annotation { "Feature Type Name" : "Feature", "Feature Type Description" : "" }
export const myFeature = defineFeature(function(context is Context, id is Id, definition is map)
    precondition{}
    {
        {
            var Q0;
            Q0=qCreatedBy(makeId("Front.planeOp"),FACE);
            var sketch = newSketch(context, id + "F0", { "sketchPlane" : qUnion([Q0])});
            skArc(sketch, "E0", {"start": v(0, -100.55) * mm, "mid": v(100.55, 0) * mm, "end": v(0, 100.55) * mm});
            skLineSegment(sketch, "E1", {"start": v(0, 0) * mm, "end": v(0, 121.6) * mm});
            skLineSegment(sketch, "E2", {"start": v(0, 0) * mm, "end": v(0, -100.55) * mm});
            skSolve(sketch);
        }
        {
            var Q0;
            Q0 = qSketchRegion(id + "F0", true);
            var Q1;
            Q1=sQuery(id+"F0.wireOp",EDGE,"E1");
            revolve(context, id + "F1", {"surfaceOperationType" : NewSurfaceOperationType.NEW, "entities" : qUnion([Q0]), "axis" : qUnion([Q1]), "revolveType" : RevolveType.FULL});
        }
        {
            var Q0;
            Q0=qCreatedBy(makeId("Right.planeOp"),FACE);
            var sketch = newSketch(context, id + "F2", { "sketchPlane" : qUnion([Q0])});
            skLineSegment(sketch, "E3.bottom", {"start": v(0, -120.65) * mm, "end": v(6045.2, -120.65) * mm});
            skLineSegment(sketch, "E3.top", {"start": v(0, -107.95) * mm, "end": v(6045.2, -107.95) * mm});
            skLineSegment(sketch, "E3.left", {"start": v(0, -120.65) * mm, "end": v(0, -107.95) * mm});
            skLineSegment(sketch, "E3.right", {"start": v(6045.2, -120.65) * mm, "end": v(6045.2, -107.95) * mm});
            skSolve(sketch);
        }
        {
            var Q0;
            Q0 = qSketchRegion(id + "F2", true);
            extrude(context, id + "F3", {"entities" : qUnion([Q0]), "depth" : 12.7 * mm, "offsetDistance" : 25.4 * mm});
        }
        {
            var Q0;
            Q0=makeQuery(id+"F3.opExtrude","CAP_FACE",FACE,{"disambiguationData":[OSD([sQuery(id+"F2.wireOp",EDGE,"E3.bottom"),sQuery(id+"F2.wireOp",EDGE,"E3.top"),sQuery(id+"F2.wireOp",EDGE,"E3.left"),sQuery(id+"F2.wireOp",EDGE,"E3.right")])],"isStart":true});
            var sketch = newSketch(context, id + "F4", { "sketchPlane" : qUnion([Q0])});
            skArc(sketch, "E4", {"start": v(-6045.12, -73.89) * mm, "mid": v(-6017.65, -46.52) * mm, "end": v(-6045.02, -19.05) * mm});
            skLineSegment(sketch, "E5", {"start": v(-6045.2, -120.65) * mm, "end": v(-6045.02, -19.05) * mm});
            skSolve(sketch);
        }
        {
            var Q0;
            Q0 = qSketchRegion(id + "F4", true);
            var Q1;
            Q1=sQuery(id+"F4.wireOp",EDGE,"E5");
            revolve(context, id + "F5", {"surfaceOperationType" : NewSurfaceOperationType.NEW, "entities" : qUnion([Q0]), "axis" : qUnion([Q1]), "revolveType" : RevolveType.FULL});
        }
        {
            var Q0;
            Q0=makeQuery(id+"F3.opExtrude","CAP_FACE",FACE,{"disambiguationData":[OSD([sQuery(id+"F2.wireOp",EDGE,"E3.bottom"),sQuery(id+"F2.wireOp",EDGE,"E3.top"),sQuery(id+"F2.wireOp",EDGE,"E3.left"),sQuery(id+"F2.wireOp",EDGE,"E3.right")])],"isStart":true});
            var sketch = newSketch(context, id + "F6", { "sketchPlane" : qUnion([Q0])});
            skLineSegment(sketch, "E6", {"start": v(-6045.2, -120.65) * mm, "end": v(-6045.2, -69.85) * mm});
            skLineSegment(sketch, "E7", {"start": v(-6045.2, -69.85) * mm, "end": v(-5957.21, -120.65) * mm});
            skLineSegment(sketch, "E8", {"start": v(0, -120.65) * mm, "end": v(0, -69.85) * mm});
            skLineSegment(sketch, "E9", {"start": v(0, -69.85) * mm, "end": v(-87.99, -120.65) * mm});
            skLineSegment(sketch, "E10", {"start": v(-87.99, -120.65) * mm, "end": v(0, -120.65) * mm});
            skLineSegment(sketch, "E11", {"start": v(-6045.2, -120.65) * mm, "end": v(-5957.21, -120.65) * mm});
            skSolve(sketch);
        }
        {
            var Q0;
            Q0 = qSketchRegion(id + "F6", true);
            extrude(context, id + "F7", {"entities" : qUnion([Q0]), "operationType" : NewBodyOperationType.ADD, "depth" : 12.7 * mm, "offsetDistance" : 25.4 * mm, "hasSecondDirection" : true, "secondDirectionOppositeDirection" : true, "secondDirectionDepth" : 12.7 * mm});
        }
        {
            var Q0;
            Q0=makeQuery(id+"F3.opExtrude","CAP_FACE",FACE,{"disambiguationData":[OSD([sQuery(id+"F2.wireOp",EDGE,"E3.bottom"),sQuery(id+"F2.wireOp",EDGE,"E3.top"),sQuery(id+"F2.wireOp",EDGE,"E3.left"),sQuery(id+"F2.wireOp",EDGE,"E3.right")])],"isStart":true});
            extrude(context, id + "F8", {"entities" : qUnion([Q0]), "operationType" : NewBodyOperationType.ADD, "depth" : 12.7 * mm, "offsetDistance" : 25.4 * mm});
        }
        {
            var Q0;
            {var subQ0=sQuery(id+"F2.wireOp",EDGE,"E3.top");Q0=makeQuery(id+"F8.boolean.opBoolean","MERGE",FACE,{"derivedFrom":[makeQuery(id+"F3.opExtrude","SWEPT_FACE",FACE,{"disambiguationData":[OSD([subQ0])]}),makeQuery(id+"F8.opExtrude","SWEPT_FACE",FACE,{"disambiguationData":[OSD([subQ0])]})]});}
            var sketch = newSketch(context, id + "F9", { "sketchPlane" : qUnion([Q0])});
            skLineSegment(sketch, "E12.bottom", {"start": v(-12.7, 101.6) * mm, "end": v(12.7, 101.6) * mm});
            skLineSegment(sketch, "E12.top", {"start": v(-12.7, 104.14) * mm, "end": v(12.7, 104.14) * mm});
            skLineSegment(sketch, "E12.left", {"start": v(-12.7, 101.6) * mm, "end": v(-12.7, 104.14) * mm});
            skLineSegment(sketch, "E12.right", {"start": v(12.7, 101.6) * mm, "end": v(12.7, 104.14) * mm});
            skSolve(sketch);
        }
        {
            var Q0;
            Q0 = qSketchRegion(id + "F9", true);
            extrude(context, id + "F10", {"entities" : qUnion([Q0]), "operationType" : NewBodyOperationType.REMOVE, "oppositeDirection" : true, "depth" : 2.54 * mm, "offsetDistance" : 25.4 * mm});
        }
        {
            var Q0;
            Q0=makeQuery(id+"F7.boolean.opBoolean","MERGE",FACE,{"derivedFrom":[makeQuery(id+"F3.opExtrude","CAP_FACE",FACE,{"disambiguationData":[OSD([sQuery(id+"F2.wireOp",EDGE,"E3.bottom"),sQuery(id+"F2.wireOp",EDGE,"E3.top"),sQuery(id+"F2.wireOp",EDGE,"E3.left"),sQuery(id+"F2.wireOp",EDGE,"E3.right")])],"isStart":false}),makeQuery(id+"F7.opExtrude","CAP_FACE",FACE,{"disambiguationData":[OSD([sQuery(id+"F6.wireOp",EDGE,"E6"),sQuery(id+"F6.wireOp",EDGE,"E7"),sQuery(id+"F6.wireOp",EDGE,"E11")])],"isStart":true}),makeQuery(id+"F7.opExtrude","CAP_FACE",FACE,{"disambiguationData":[OSD([sQuery(id+"F6.wireOp",EDGE,"E8"),sQuery(id+"F6.wireOp",EDGE,"E9"),sQuery(id+"F6.wireOp",EDGE,"E10")])],"isStart":true})]});
            var sketch = newSketch(context, id + "F11", { "sketchPlane" : qUnion([Q0])});
            skText(sketch, "E13", { "text": "          Low Earth Orbit\n(International Space Station)", "fontName": "OpenSans-Regular.ttf"});
            const initialGuessF11  = {"E13": [0.08123, -0.11366, 1, 0, 0.00254]};
            skSetInitialGuess(sketch, initialGuessF11);
            skSolve(sketch);
        }
        {
            var Q0;
            Q0 = qSketchRegion(id + "F11", true);
            extrude(context, id + "F12", {"entities" : qUnion([Q0]), "operationType" : NewBodyOperationType.REMOVE, "oppositeDirection" : true, "depth" : 2.54 * mm, "offsetDistance" : 25.4 * mm});
        }
        {
            var Q0;
            {var subQ0=sQuery(id+"F2.wireOp",EDGE,"E3.right");var subQ3=sQuery(id+"F2.wireOp",EDGE,"E3.left");var subQ4=sQuery(id+"F2.wireOp",EDGE,"E3.top");var subQ5=sQuery(id+"F2.wireOp",EDGE,"E3.bottom");var subQ6=sQuery(id+"F6.wireOp",EDGE,"E11");var subQ7=sQuery(id+"F6.wireOp",EDGE,"E10");var subQ8=sQuery(id+"F6.wireOp",EDGE,"E7");var subQ9=sQuery(id+"F6.wireOp",EDGE,"E8");var subQ10=sQuery(id+"F6.wireOp",EDGE,"E9");var subQ11=sQuery(id+"F6.wireOp",EDGE,"E6");Q0=makeQuery(id+"F12.boolean.opBoolean","SPLIT",FACE,{"disambiguationData":[TD([makeQuery(id+"F1.opRevolve","SWEPT_FACE",FACE,{"disambiguationData":[OSD([sQuery(id+"F0.wireOp",EDGE,"E0")])]})])],"derivedFrom":makeQuery(id+"F7.boolean.opBoolean","MERGE",FACE,{"derivedFrom":[makeQuery(id+"F3.opExtrude","CAP_FACE",FACE,{"disambiguationData":[OSD([subQ5,subQ4,subQ3,subQ0])],"isStart":false}),makeQuery(id+"F7.opExtrude","CAP_FACE",FACE,{"disambiguationData":[OSD([subQ11,subQ8,subQ6])],"isStart":true}),makeQuery(id+"F7.opExtrude","CAP_FACE",FACE,{"disambiguationData":[OSD([subQ9,subQ10,subQ7])],"isStart":true})]})});}
            var sketch = newSketch(context, id + "F13", { "sketchPlane" : qUnion([Q0])});
            skLineSegment(sketch, "E14.bottom", {"start": v(660.4, -107.95) * mm, "end": v(662.94, -107.95) * mm});
            skLineSegment(sketch, "E14.top", {"start": v(660.4, -110.49) * mm, "end": v(662.94, -110.49) * mm});
            skLineSegment(sketch, "E14.left", {"start": v(660.4, -107.95) * mm, "end": v(660.4, -110.49) * mm});
            skLineSegment(sketch, "E14.right", {"start": v(662.94, -107.95) * mm, "end": v(662.94, -110.49) * mm});
            skSolve(sketch);
        }
        {
            var Q0;
            Q0 = qSketchRegion(id + "F13", true);
            extrude(context, id + "F14", {"entities" : qUnion([Q0]), "operationType" : NewBodyOperationType.REMOVE, "endBound" : BoundingType.THROUGH_ALL, "oppositeDirection" : true, "depth" : 25.4 * mm, "offsetDistance" : 25.4 * mm});
        }
        {
            var Q0;
            {var subQ0=sQuery(id+"F2.wireOp",EDGE,"E3.right");var subQ3=sQuery(id+"F2.wireOp",EDGE,"E3.left");var subQ4=sQuery(id+"F2.wireOp",EDGE,"E3.top");var subQ5=sQuery(id+"F2.wireOp",EDGE,"E3.bottom");var subQ6=sQuery(id+"F6.wireOp",EDGE,"E11");var subQ7=sQuery(id+"F6.wireOp",EDGE,"E10");var subQ8=sQuery(id+"F6.wireOp",EDGE,"E7");var subQ9=sQuery(id+"F6.wireOp",EDGE,"E8");var subQ10=sQuery(id+"F6.wireOp",EDGE,"E9");var subQ11=sQuery(id+"F6.wireOp",EDGE,"E6");Q0=makeQuery(id+"F12.boolean.opBoolean","SPLIT",FACE,{"disambiguationData":[TD([makeQuery(id+"F1.opRevolve","SWEPT_FACE",FACE,{"disambiguationData":[OSD([sQuery(id+"F0.wireOp",EDGE,"E0")])]})])],"derivedFrom":makeQuery(id+"F7.boolean.opBoolean","MERGE",FACE,{"derivedFrom":[makeQuery(id+"F3.opExtrude","CAP_FACE",FACE,{"disambiguationData":[OSD([subQ5,subQ4,subQ3,subQ0])],"isStart":false}),makeQuery(id+"F7.opExtrude","CAP_FACE",FACE,{"disambiguationData":[OSD([subQ11,subQ8,subQ6])],"isStart":true}),makeQuery(id+"F7.opExtrude","CAP_FACE",FACE,{"disambiguationData":[OSD([subQ9,subQ10,subQ7])],"isStart":true})]})});}
            var sketch = newSketch(context, id + "F15", { "sketchPlane" : qUnion([Q0])});
            skText(sketch, "E15", { "text": "     Geosynchronous Orbit\n(GPS and Television Satellites)", "fontName": "OpenSans-Regular.ttf"});
            const initialGuessF15  = {"E15": [0.63754, -0.11366, 1, 0, 0.00254]};
            skSetInitialGuess(sketch, initialGuessF15);
            skSolve(sketch);
        }
        {
            var Q0;
            Q0 = qSketchRegion(id + "F15", true);
            extrude(context, id + "F16", {"entities" : qUnion([Q0]), "operationType" : NewBodyOperationType.REMOVE, "oppositeDirection" : true, "depth" : 2.54 * mm, "offsetDistance" : 25.4 * mm});
        }
        {
            var Q0;
            {var subQ278=sQuery(id+"F6.wireOp",EDGE,"E10");var subQ282=sQuery(id+"F6.wireOp",EDGE,"E7");var subQ290=sQuery(id+"F6.wireOp",EDGE,"E9");var subQ297=sQuery(id+"F6.wireOp",EDGE,"E6");var subQ304=sQuery(id+"F6.wireOp",EDGE,"E8");var subQ343=sQuery(id+"F2.wireOp",EDGE,"E3.right");var subQ356=sQuery(id+"F2.wireOp",EDGE,"E3.top");var subQ379=sQuery(id+"F6.wireOp",EDGE,"E11");var subQ384=sQuery(id+"F2.wireOp",EDGE,"E3.bottom");var subQ396=sQuery(id+"F2.wireOp",EDGE,"E3.left");var subQ507=makeQuery(id+"F1.opRevolve","SWEPT_FACE",FACE,{"disambiguationData":[OSD([sQuery(id+"F0.wireOp",EDGE,"E0")])]});Q0=makeQuery(id+"F16.boolean.opBoolean","SPLIT",FACE,{"disambiguationData":[TD([subQ507])],"derivedFrom":makeQuery(id+"F12.boolean.opBoolean","SPLIT",FACE,{"disambiguationData":[TD([subQ507])],"derivedFrom":makeQuery(id+"F7.boolean.opBoolean","MERGE",FACE,{"derivedFrom":[makeQuery(id+"F3.opExtrude","CAP_FACE",FACE,{"disambiguationData":[OSD([subQ384,subQ356,subQ396,subQ343])],"isStart":false}),makeQuery(id+"F7.opExtrude","CAP_FACE",FACE,{"disambiguationData":[OSD([subQ297,subQ282,subQ379])],"isStart":true}),makeQuery(id+"F7.opExtrude","CAP_FACE",FACE,{"disambiguationData":[OSD([subQ304,subQ290,subQ278])],"isStart":true})]})})});}
            var sketch = newSketch(context, id + "F17", { "sketchPlane" : qUnion([Q0])});
            skLineSegment(sketch, "E16.bottom", {"start": v(1143, -107.95) * mm, "end": v(1145.54, -107.95) * mm});
            skLineSegment(sketch, "E16.top", {"start": v(1143, -110.49) * mm, "end": v(1145.54, -110.49) * mm});
            skLineSegment(sketch, "E16.left", {"start": v(1143, -107.95) * mm, "end": v(1143, -110.49) * mm});
            skLineSegment(sketch, "E16.right", {"start": v(1145.54, -107.95) * mm, "end": v(1145.54, -110.49) * mm});
            skSolve(sketch);
        }
        {
            var Q0;
            Q0 = qSketchRegion(id + "F17", true);
            extrude(context, id + "F18", {"entities" : qUnion([Q0]), "operationType" : NewBodyOperationType.REMOVE, "oppositeDirection" : true, "depth" : 25.4 * mm, "offsetDistance" : 25.4 * mm});
        }
        {
            var Q0;
            {var subQ278=sQuery(id+"F6.wireOp",EDGE,"E10");var subQ282=sQuery(id+"F6.wireOp",EDGE,"E7");var subQ290=sQuery(id+"F6.wireOp",EDGE,"E9");var subQ297=sQuery(id+"F6.wireOp",EDGE,"E6");var subQ304=sQuery(id+"F6.wireOp",EDGE,"E8");var subQ343=sQuery(id+"F2.wireOp",EDGE,"E3.right");var subQ356=sQuery(id+"F2.wireOp",EDGE,"E3.top");var subQ379=sQuery(id+"F6.wireOp",EDGE,"E11");var subQ384=sQuery(id+"F2.wireOp",EDGE,"E3.bottom");var subQ396=sQuery(id+"F2.wireOp",EDGE,"E3.left");var subQ507=makeQuery(id+"F1.opRevolve","SWEPT_FACE",FACE,{"disambiguationData":[OSD([sQuery(id+"F0.wireOp",EDGE,"E0")])]});Q0=makeQuery(id+"F16.boolean.opBoolean","SPLIT",FACE,{"disambiguationData":[TD([subQ507])],"derivedFrom":makeQuery(id+"F12.boolean.opBoolean","SPLIT",FACE,{"disambiguationData":[TD([subQ507])],"derivedFrom":makeQuery(id+"F7.boolean.opBoolean","MERGE",FACE,{"derivedFrom":[makeQuery(id+"F3.opExtrude","CAP_FACE",FACE,{"disambiguationData":[OSD([subQ384,subQ356,subQ396,subQ343])],"isStart":false}),makeQuery(id+"F7.opExtrude","CAP_FACE",FACE,{"disambiguationData":[OSD([subQ297,subQ282,subQ379])],"isStart":true}),makeQuery(id+"F7.opExtrude","CAP_FACE",FACE,{"disambiguationData":[OSD([subQ304,subQ290,subQ278])],"isStart":true})]})})});}
            var sketch = newSketch(context, id + "F19", { "sketchPlane" : qUnion([Q0])});
            skText(sketch, "E17", { "text": "Van Allen Belt", "fontName": "OpenSans-Regular.ttf"});
            const initialGuessF19  = {"E17": [1.13288, -0.11366, 1, 0, 0.00254]};
            skSetInitialGuess(sketch, initialGuessF19);
            skSolve(sketch);
        }
        {
            var Q0;
            Q0 = qSketchRegion(id + "F19", true);
            extrude(context, id + "F20", {"entities" : qUnion([Q0]), "operationType" : NewBodyOperationType.REMOVE, "oppositeDirection" : true, "depth" : 2.54 * mm, "offsetDistance" : 25.4 * mm});
        }
    });